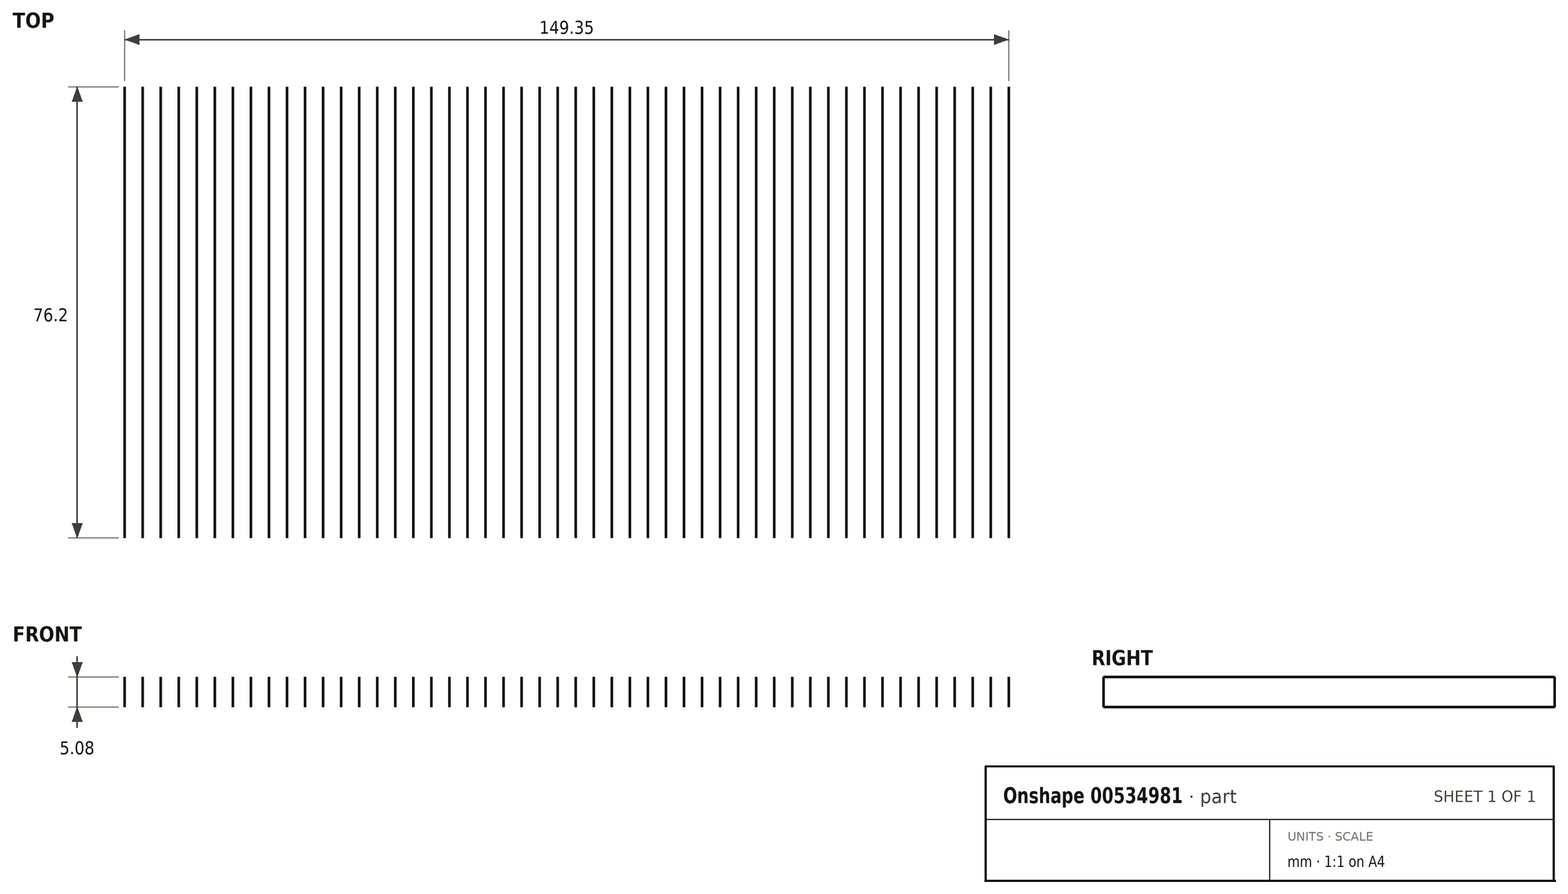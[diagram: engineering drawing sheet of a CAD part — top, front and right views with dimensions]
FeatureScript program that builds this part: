
annotation { "Feature Type Name" : "Feature", "Feature Type Description" : "" }
export const myFeature = defineFeature(function(context is Context, id is Id, definition is map)
    precondition{}
    {
        {
            var Q0;
            Q0=qCreatedBy(makeId("Top.planeOp"),FACE);
            var sketch = newSketch(context, id + "F0", { "sketchPlane" : qUnion([Q0])});
            skLineSegment(sketch, "E0", {"start": v(-76.3, 38.1) * mm, "end": v(-76.3, -38.1) * mm});
            skLineSegment(sketch, "E1.1.0.0", {"start": v(-73.26, 38.1) * mm, "end": v(-73.26, -38.1) * mm});
            skLineSegment(sketch, "E1.2.0.0", {"start": v(-70.2, 38.1) * mm, "end": v(-70.2, -38.1) * mm});
            skLineSegment(sketch, "E1.3.0.0", {"start": v(-67.16, 38.1) * mm, "end": v(-67.16, -38.1) * mm});
            skLineSegment(sketch, "E1.4.0.0", {"start": v(-64.11, 38.1) * mm, "end": v(-64.11, -38.1) * mm});
            skLineSegment(sketch, "E1.5.0.0", {"start": v(-61.06, 38.1) * mm, "end": v(-61.06, -38.1) * mm});
            skLineSegment(sketch, "E1.6.0.0", {"start": v(-58.02, 38.1) * mm, "end": v(-58.02, -38.1) * mm});
            skLineSegment(sketch, "E1.7.0.0", {"start": v(-54.97, 38.1) * mm, "end": v(-54.97, -38.1) * mm});
            skLineSegment(sketch, "E1.8.0.0", {"start": v(-51.92, 38.1) * mm, "end": v(-51.92, -38.1) * mm});
            skLineSegment(sketch, "E1.9.0.0", {"start": v(-48.87, 38.1) * mm, "end": v(-48.87, -38.1) * mm});
            skLineSegment(sketch, "E1.10.0.0", {"start": v(-45.82, 38.1) * mm, "end": v(-45.82, -38.1) * mm});
            skLineSegment(sketch, "E1.11.0.0", {"start": v(-42.78, 38.1) * mm, "end": v(-42.78, -38.1) * mm});
            skLineSegment(sketch, "E1.12.0.0", {"start": v(-39.73, 38.1) * mm, "end": v(-39.73, -38.1) * mm});
            skLineSegment(sketch, "E1.13.0.0", {"start": v(-36.68, 38.1) * mm, "end": v(-36.68, -38.1) * mm});
            skLineSegment(sketch, "E1.14.0.0", {"start": v(-33.63, 38.1) * mm, "end": v(-33.63, -38.1) * mm});
            skLineSegment(sketch, "E1.15.0.0", {"start": v(-30.58, 38.1) * mm, "end": v(-30.58, -38.1) * mm});
            skLineSegment(sketch, "E1.16.0.0", {"start": v(-27.54, 38.1) * mm, "end": v(-27.54, -38.1) * mm});
            skLineSegment(sketch, "E1.17.0.0", {"start": v(-24.49, 38.1) * mm, "end": v(-24.49, -38.1) * mm});
            skLineSegment(sketch, "E1.18.0.0", {"start": v(-21.44, 38.1) * mm, "end": v(-21.44, -38.1) * mm});
            skLineSegment(sketch, "E1.19.0.0", {"start": v(-18.4, 38.1) * mm, "end": v(-18.4, -38.1) * mm});
            skLineSegment(sketch, "E1.20.0.0", {"start": v(-15.34, 38.1) * mm, "end": v(-15.34, -38.1) * mm});
            skLineSegment(sketch, "E1.21.0.0", {"start": v(-12.3, 38.1) * mm, "end": v(-12.3, -38.1) * mm});
            skLineSegment(sketch, "E1.22.0.0", {"start": v(-9.25, 38.1) * mm, "end": v(-9.25, -38.1) * mm});
            skLineSegment(sketch, "E1.23.0.0", {"start": v(-6.2, 38.1) * mm, "end": v(-6.2, -38.1) * mm});
            skLineSegment(sketch, "E1.24.0.0", {"start": v(-3.15, 38.1) * mm, "end": v(-3.15, -38.1) * mm});
            skLineSegment(sketch, "E1.25.0.0", {"start": v(-0.1, 38.1) * mm, "end": v(-0.1, -38.1) * mm});
            skLineSegment(sketch, "E1.26.0.0", {"start": v(2.94, 38.1) * mm, "end": v(2.94, -38.1) * mm});
            skLineSegment(sketch, "E1.27.0.0", {"start": v(6, 38.1) * mm, "end": v(6, -38.1) * mm});
            skLineSegment(sketch, "E1.28.0.0", {"start": v(9.04, 38.1) * mm, "end": v(9.04, -38.1) * mm});
            skLineSegment(sketch, "E1.29.0.0", {"start": v(12.09, 38.1) * mm, "end": v(12.09, -38.1) * mm});
            skLineSegment(sketch, "E1.30.0.0", {"start": v(15.14, 38.1) * mm, "end": v(15.14, -38.1) * mm});
            skLineSegment(sketch, "E1.31.0.0", {"start": v(18.18, 38.1) * mm, "end": v(18.18, -38.1) * mm});
            skLineSegment(sketch, "E1.32.0.0", {"start": v(21.23, 38.1) * mm, "end": v(21.23, -38.1) * mm});
            skLineSegment(sketch, "E1.33.0.0", {"start": v(24.28, 38.1) * mm, "end": v(24.28, -38.1) * mm});
            skLineSegment(sketch, "E1.34.0.0", {"start": v(27.33, 38.1) * mm, "end": v(27.33, -38.1) * mm});
            skLineSegment(sketch, "E1.35.0.0", {"start": v(30.38, 38.1) * mm, "end": v(30.38, -38.1) * mm});
            skLineSegment(sketch, "E1.36.0.0", {"start": v(33.42, 38.1) * mm, "end": v(33.42, -38.1) * mm});
            skLineSegment(sketch, "E1.37.0.0", {"start": v(36.47, 38.1) * mm, "end": v(36.47, -38.1) * mm});
            skLineSegment(sketch, "E1.38.0.0", {"start": v(39.52, 38.1) * mm, "end": v(39.52, -38.1) * mm});
            skLineSegment(sketch, "E1.39.0.0", {"start": v(42.57, 38.1) * mm, "end": v(42.57, -38.1) * mm});
            skLineSegment(sketch, "E1.40.0.0", {"start": v(45.62, 38.1) * mm, "end": v(45.62, -38.1) * mm});
            skLineSegment(sketch, "E1.41.0.0", {"start": v(48.66, 38.1) * mm, "end": v(48.66, -38.1) * mm});
            skLineSegment(sketch, "E1.42.0.0", {"start": v(51.71, 38.1) * mm, "end": v(51.71, -38.1) * mm});
            skLineSegment(sketch, "E1.43.0.0", {"start": v(54.76, 38.1) * mm, "end": v(54.76, -38.1) * mm});
            skLineSegment(sketch, "E1.44.0.0", {"start": v(57.8, 38.1) * mm, "end": v(57.8, -38.1) * mm});
            skLineSegment(sketch, "E1.45.0.0", {"start": v(60.86, 38.1) * mm, "end": v(60.86, -38.1) * mm});
            skLineSegment(sketch, "E1.46.0.0", {"start": v(63.9, 38.1) * mm, "end": v(63.9, -38.1) * mm});
            skLineSegment(sketch, "E1.47.0.0", {"start": v(66.95, 38.1) * mm, "end": v(66.95, -38.1) * mm});
            skLineSegment(sketch, "E1.48.0.0", {"start": v(70, 38.1) * mm, "end": v(70, -38.1) * mm});
            skLineSegment(sketch, "E1.49.0.0", {"start": v(73.05, 38.1) * mm, "end": v(73.05, -38.1) * mm});
            skLineSegment(sketch, "E1.direction1", {"start": v(-76.3, -38.1) * mm, "end": v(-73.26, -38.1) * mm, "construction": true});
            skSolve(sketch);
        }
        {
            var Q0;
            Q0=sQuery(id+"F0.wireOp",EDGE,"E1.41.0.0");
            var Q1;
            Q1=sQuery(id+"F0.wireOp",EDGE,"E1.34.0.0");
            var Q2;
            Q2=sQuery(id+"F0.wireOp",EDGE,"E1.25.0.0");
            var Q3;
            Q3=sQuery(id+"F0.wireOp",EDGE,"E1.18.0.0");
            var Q4;
            Q4=sQuery(id+"F0.wireOp",EDGE,"E1.33.0.0");
            var Q5;
            Q5=sQuery(id+"F0.wireOp",EDGE,"E1.49.0.0");
            var Q6;
            Q6=sQuery(id+"F0.wireOp",EDGE,"E1.17.0.0");
            var Q7;
            Q7=sQuery(id+"F0.wireOp",EDGE,"E1.24.0.0");
            var Q8;
            Q8=sQuery(id+"F0.wireOp",EDGE,"E1.40.0.0");
            var Q9;
            Q9=sQuery(id+"F0.wireOp",EDGE,"E1.32.0.0");
            var Q10;
            Q10=sQuery(id+"F0.wireOp",EDGE,"E1.48.0.0");
            var Q11;
            Q11=sQuery(id+"F0.wireOp",EDGE,"E1.16.0.0");
            var Q12;
            Q12=sQuery(id+"F0.wireOp",EDGE,"E1.23.0.0");
            var Q13;
            Q13=sQuery(id+"F0.wireOp",EDGE,"E1.39.0.0");
            var Q14;
            Q14=sQuery(id+"F0.wireOp",EDGE,"E1.12.0.0");
            var Q15;
            Q15=sQuery(id+"F0.wireOp",EDGE,"E1.11.0.0");
            var Q16;
            Q16=sQuery(id+"F0.wireOp",EDGE,"E1.10.0.0");
            var Q17;
            Q17=sQuery(id+"F0.wireOp",EDGE,"E1.9.0.0");
            var Q18;
            Q18=sQuery(id+"F0.wireOp",EDGE,"E1.8.0.0");
            var Q19;
            Q19=sQuery(id+"F0.wireOp",EDGE,"E1.7.0.0");
            var Q20;
            Q20=sQuery(id+"F0.wireOp",EDGE,"E1.6.0.0");
            var Q21;
            Q21=sQuery(id+"F0.wireOp",EDGE,"E1.5.0.0");
            var Q22;
            Q22=sQuery(id+"F0.wireOp",EDGE,"E1.4.0.0");
            var Q23;
            Q23=sQuery(id+"F0.wireOp",EDGE,"E1.3.0.0");
            var Q24;
            Q24=sQuery(id+"F0.wireOp",EDGE,"E1.2.0.0");
            var Q25;
            Q25=sQuery(id+"F0.wireOp",EDGE,"E1.1.0.0");
            var Q26;
            Q26=sQuery(id+"F0.wireOp",EDGE,"E0");
            var Q27;
            Q27=sQuery(id+"F0.wireOp",EDGE,"E1.15.0.0");
            var Q28;
            Q28=sQuery(id+"F0.wireOp",EDGE,"E1.14.0.0");
            var Q29;
            Q29=sQuery(id+"F0.wireOp",EDGE,"E1.13.0.0");
            var Q30;
            Q30=sQuery(id+"F0.wireOp",EDGE,"E1.31.0.0");
            var Q31;
            Q31=sQuery(id+"F0.wireOp",EDGE,"E1.38.0.0");
            var Q32;
            Q32=sQuery(id+"F0.wireOp",EDGE,"E1.47.0.0");
            var Q33;
            Q33=sQuery(id+"F0.wireOp",EDGE,"E1.22.0.0");
            var Q34;
            Q34=sQuery(id+"F0.wireOp",EDGE,"E1.30.0.0");
            var Q35;
            Q35=sQuery(id+"F0.wireOp",EDGE,"E1.37.0.0");
            var Q36;
            Q36=sQuery(id+"F0.wireOp",EDGE,"E1.46.0.0");
            var Q37;
            Q37=sQuery(id+"F0.wireOp",EDGE,"E1.21.0.0");
            var Q38;
            Q38=sQuery(id+"F0.wireOp",EDGE,"E1.28.0.0");
            var Q39;
            Q39=sQuery(id+"F0.wireOp",EDGE,"E1.44.0.0");
            var Q40;
            Q40=sQuery(id+"F0.wireOp",EDGE,"E1.29.0.0");
            var Q41;
            Q41=sQuery(id+"F0.wireOp",EDGE,"E1.36.0.0");
            var Q42;
            Q42=sQuery(id+"F0.wireOp",EDGE,"E1.45.0.0");
            var Q43;
            Q43=sQuery(id+"F0.wireOp",EDGE,"E1.20.0.0");
            var Q44;
            Q44=sQuery(id+"F0.wireOp",EDGE,"E1.27.0.0");
            var Q45;
            Q45=sQuery(id+"F0.wireOp",EDGE,"E1.43.0.0");
            var Q46;
            Q46=sQuery(id+"F0.wireOp",EDGE,"E1.35.0.0");
            var Q47;
            Q47=sQuery(id+"F0.wireOp",EDGE,"E1.19.0.0");
            var Q48;
            Q48=sQuery(id+"F0.wireOp",EDGE,"E1.26.0.0");
            var Q49;
            Q49=sQuery(id+"F0.wireOp",EDGE,"E1.42.0.0");
            extrude(context, id + "F1", {"bodyType" : ToolBodyType.SURFACE, "surfaceEntities" : qUnion([Q0, Q1, Q2, Q3, Q4, Q5, Q6, Q7, Q8, Q9, Q10, Q11, Q12, Q13, Q14, Q15, Q16, Q17, Q18, Q19, Q20, Q21, Q22, Q23, Q24, Q25, Q26, Q27, Q28, Q29, Q30, Q31, Q32, Q33, Q34, Q35, Q36, Q37, Q38, Q39, Q40, Q41, Q42, Q43, Q44, Q45, Q46, Q47, Q48, Q49]), "depth" : 5.08 * mm, "offsetDistance" : 25.4 * mm});
        }
    });
